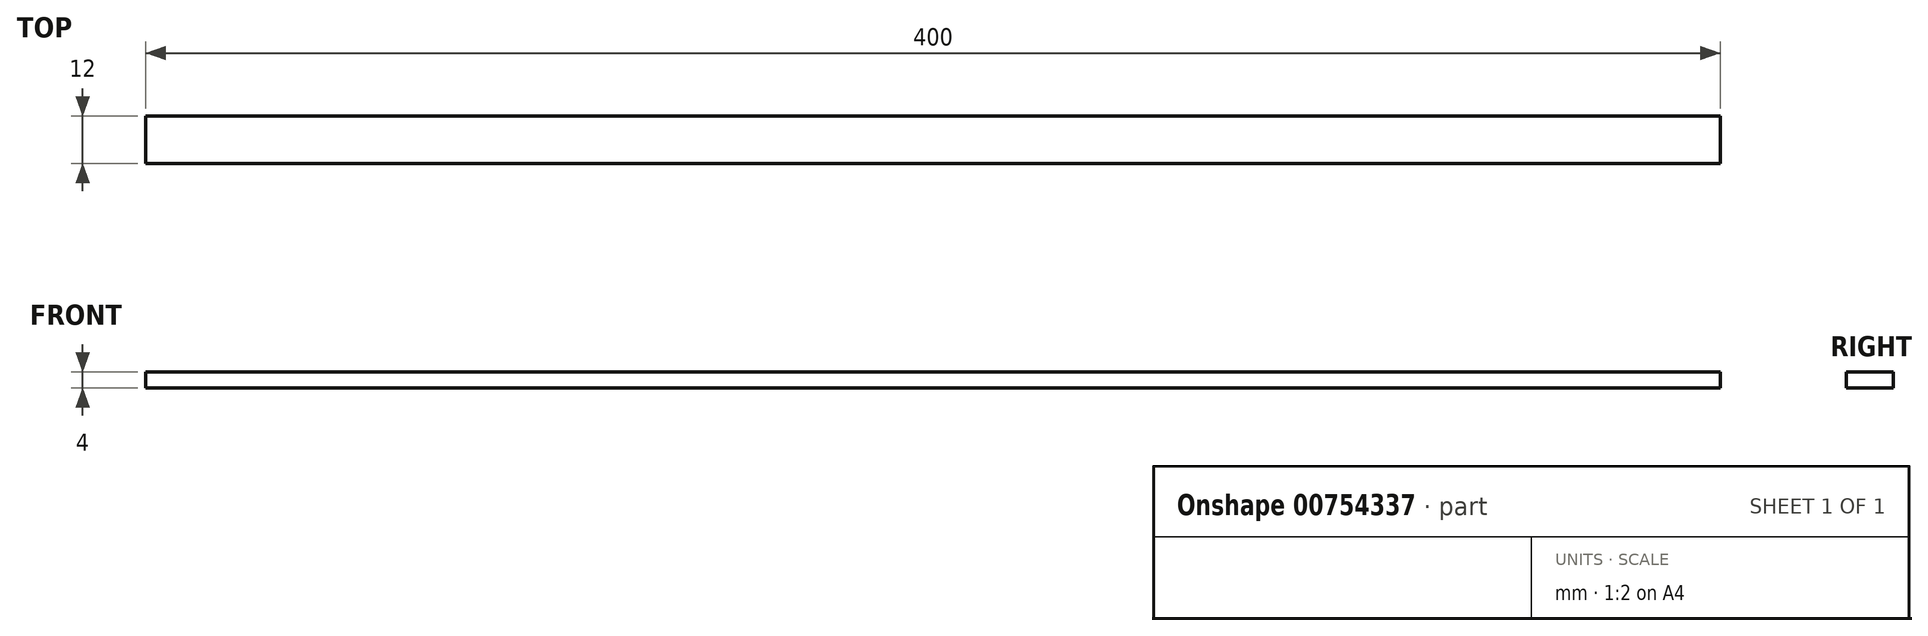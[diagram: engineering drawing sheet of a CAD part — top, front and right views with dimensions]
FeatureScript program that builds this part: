
annotation { "Feature Type Name" : "Feature", "Feature Type Description" : "" }
export const myFeature = defineFeature(function(context is Context, id is Id, definition is map)
    precondition{}
    {
        {
            var Q0;
            Q0=qCreatedBy(makeId("Right.planeOp"),FACE);
            var sketch = newSketch(context, id + "F0", { "sketchPlane" : qUnion([Q0])});
            skLineSegment(sketch, "E0.bottom", {"start": v(6, -2) * mm, "end": v(-6, -2) * mm});
            skLineSegment(sketch, "E0.top", {"start": v(6, 2) * mm, "end": v(-6, 2) * mm});
            skLineSegment(sketch, "E0.left", {"start": v(6, -2) * mm, "end": v(6, 2) * mm});
            skLineSegment(sketch, "E0.right", {"start": v(-6, -2) * mm, "end": v(-6, 2) * mm});
            skPoint(sketch, "E0.middle", {"position": v(0, 0) * mm});
            skSolve(sketch);
        }
        {
            var Q0;
            Q0 = qSketchRegion(id + "F0", true);
            extrude(context, id + "F1", {"entities" : qUnion([Q0]), "depth" : 400 * mm, "offsetDistance" : 25 * mm});
        }
    });
